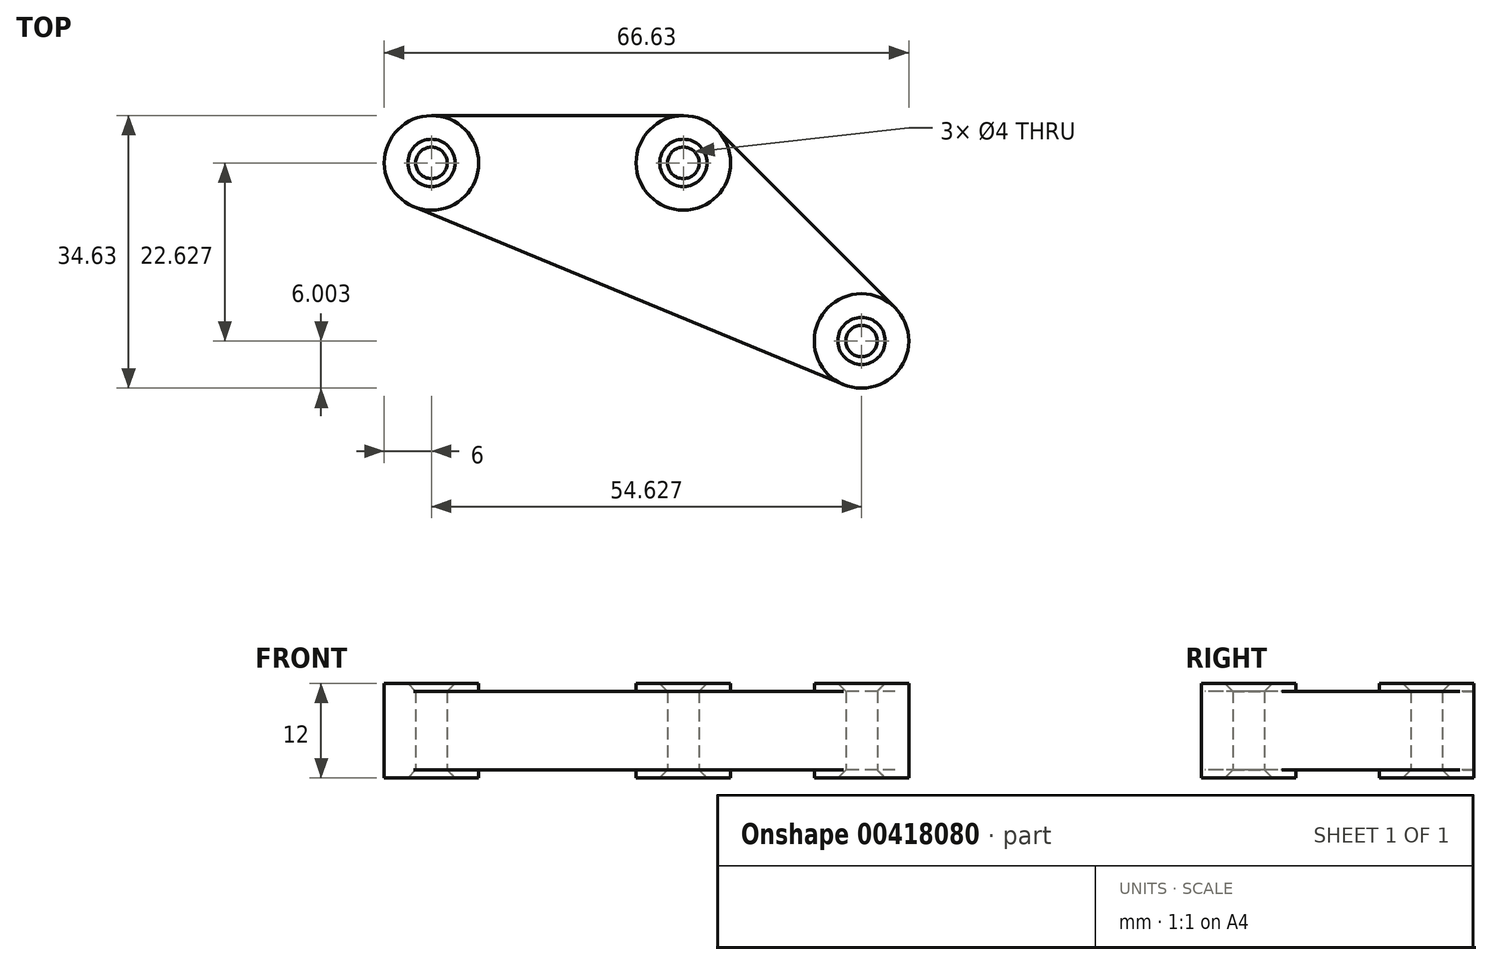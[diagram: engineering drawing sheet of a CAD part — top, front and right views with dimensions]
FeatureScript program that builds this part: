
annotation { "Feature Type Name" : "Feature", "Feature Type Description" : "" }
export const myFeature = defineFeature(function(context is Context, id is Id, definition is map)
    precondition{}
    {
        {
            var Q0;
            Q0=qCreatedBy(makeId("Top.planeOp"),FACE);
            var sketch = newSketch(context, id + "F0", { "sketchPlane" : qUnion([Q0])});
            skCircle(sketch, "E0", {"center": v(0, 0) * mm, "radius": 6 * mm});
            skCircle(sketch, "E1.1.0.0", {"center": v(32, 0) * mm, "radius": 6 * mm});
            skLineSegment(sketch, "E1.direction1", {"start": v(0, 0) * mm, "end": v(32, 0) * mm, "construction": true});
            skCircle(sketch, "E2", {"center": v(0, 0) * mm, "radius": 2 * mm});
            skCircle(sketch, "E3", {"center": v(32, 0) * mm, "radius": 2 * mm});
            skLineSegment(sketch, "E4", {"start": v(0, 0) * mm, "end": v(32, 0) * mm});
            skLineSegment(sketch, "E5", {"start": v(32, 0) * mm, "end": v(54.63, -22.63) * mm});
            skCircle(sketch, "E6", {"center": v(54.63, -22.63) * mm, "radius": 6 * mm});
            skCircle(sketch, "E7", {"center": v(54.63, -22.63) * mm, "radius": 2 * mm});
            skLineSegment(sketch, "E8", {"start": v(-2.3, -5.54) * mm, "end": v(52.33, -28.17) * mm});
            skLineSegment(sketch, "E9", {"start": v(58.87, -18.38) * mm, "end": v(36.24, 4.24) * mm});
            skLineSegment(sketch, "E10", {"start": v(0, 6) * mm, "end": v(32, 6) * mm});
            skSolve(sketch);
        }
        {
            var Q0;
            {var subQ9=sQuery(id+"F0.wireOp",EDGE,"E8");Q0=makeQuery(id+"F0.imprint","IMPRINT",FACE,{"disambiguationData":[TD([[makeQuery(id+"F0.imprint","IMPRINT",EDGE,{"derivedFrom":subQ9}),1.0]])]});}
            var Q1;
            {var subQ0=sQuery(id+"F0.wireOp",EDGE,"E10");Q1=makeQuery(id+"F0.imprint","IMPRINT",FACE,{"disambiguationData":[TD([[makeQuery(id+"F0.imprint","IMPRINT",EDGE,{"derivedFrom":subQ0}),-1.0]])]});}
            var Q2;
            {var subQ0=sQuery(id+"F0.wireOp",EDGE,"E9");Q2=makeQuery(id+"F0.imprint","IMPRINT",FACE,{"disambiguationData":[TD([[makeQuery(id+"F0.imprint","IMPRINT",EDGE,{"derivedFrom":subQ0}),1.0]])]});}
            var Q3;
            Q3=makeQuery(id+"F0.imprint","IMPRINT",FACE,{"disambiguationData":[TD([[makeQuery(id+"F0.imprint","IMPRINT",EDGE,{"derivedFrom":sQuery(id+"F0.wireOp",EDGE,"E2")}),-1.0]])]});
            var Q4;
            {var subQ0=sQuery(id+"F0.wireOp",EDGE,"E4");var subQ1=sQuery(id+"F0.wireOp",EDGE,"E1.1.0.0");var subQ2=makeQuery(id+"F0.imprint","INTERSECT",VERTEX,{"derivedFrom":[subQ1,subQ0]});Q4=makeQuery(id+"F0.imprint","IMPRINT",FACE,{"disambiguationData":[TD([[makeQuery(id+"F0.imprint","IMPRINT",EDGE,{"disambiguationData":[TD([[subQ2,-1.0]])],"derivedFrom":subQ1}),1.0]])]});}
            var Q5;
            {var subQ0=sQuery(id+"F0.wireOp",EDGE,"E1.1.0.0");var subQ1=makeQuery(id+"F0.imprint","INTERSECT",VERTEX,{"derivedFrom":[subQ0,sQuery(id+"F0.wireOp",EDGE,"E9")]});Q5=makeQuery(id+"F0.imprint","IMPRINT",FACE,{"disambiguationData":[TD([[makeQuery(id+"F0.imprint","IMPRINT",EDGE,{"disambiguationData":[TD([[subQ1,-1.0]])],"derivedFrom":subQ0}),1.0]])]});}
            var Q6;
            Q6=makeQuery(id+"F0.imprint","IMPRINT",FACE,{"disambiguationData":[TD([[makeQuery(id+"F0.imprint","IMPRINT",EDGE,{"derivedFrom":sQuery(id+"F0.wireOp",EDGE,"E7")}),-1.0]])]});
            extrude(context, id + "F1", {"entities" : qUnion([Q0, Q1, Q2, Q3, Q4, Q5, Q6]), "depth" : 10 * mm});
        }
        {
            var Q0;
            Q0=makeQuery(id+"F0.imprint","IMPRINT",FACE,{"disambiguationData":[TD([[makeQuery(id+"F0.imprint","IMPRINT",EDGE,{"derivedFrom":sQuery(id+"F0.wireOp",EDGE,"E2")}),-1.0]])]});
            var Q1;
            {var subQ0=sQuery(id+"F0.wireOp",EDGE,"E1.1.0.0");var subQ1=makeQuery(id+"F0.imprint","INTERSECT",VERTEX,{"derivedFrom":[subQ0,sQuery(id+"F0.wireOp",EDGE,"E9")]});Q1=makeQuery(id+"F0.imprint","IMPRINT",FACE,{"disambiguationData":[TD([[makeQuery(id+"F0.imprint","IMPRINT",EDGE,{"disambiguationData":[TD([[subQ1,-1.0]])],"derivedFrom":subQ0}),1.0]])]});}
            var Q2;
            {var subQ0=sQuery(id+"F0.wireOp",EDGE,"E4");var subQ1=sQuery(id+"F0.wireOp",EDGE,"E1.1.0.0");var subQ2=makeQuery(id+"F0.imprint","INTERSECT",VERTEX,{"derivedFrom":[subQ1,subQ0]});Q2=makeQuery(id+"F0.imprint","IMPRINT",FACE,{"disambiguationData":[TD([[makeQuery(id+"F0.imprint","IMPRINT",EDGE,{"disambiguationData":[TD([[subQ2,-1.0]])],"derivedFrom":subQ1}),1.0]])]});}
            var Q3;
            Q3=makeQuery(id+"F0.imprint","IMPRINT",FACE,{"disambiguationData":[TD([[makeQuery(id+"F0.imprint","IMPRINT",EDGE,{"derivedFrom":sQuery(id+"F0.wireOp",EDGE,"E7")}),-1.0]])]});
            extrude(context, id + "F2", {"entities" : qUnion([Q0, Q1, Q2, Q3]), "depth" : 11 * mm});
        }
        {
            var Q0;
            Q0=makeQuery(id+"F0.imprint","IMPRINT",FACE,{"disambiguationData":[TD([[makeQuery(id+"F0.imprint","IMPRINT",EDGE,{"derivedFrom":sQuery(id+"F0.wireOp",EDGE,"E2")}),-1.0]])]});
            var Q1;
            {var subQ0=sQuery(id+"F0.wireOp",EDGE,"E1.1.0.0");var subQ1=makeQuery(id+"F0.imprint","INTERSECT",VERTEX,{"derivedFrom":[subQ0,sQuery(id+"F0.wireOp",EDGE,"E9")]});Q1=makeQuery(id+"F0.imprint","IMPRINT",FACE,{"disambiguationData":[TD([[makeQuery(id+"F0.imprint","IMPRINT",EDGE,{"disambiguationData":[TD([[subQ1,-1.0]])],"derivedFrom":subQ0}),1.0]])]});}
            var Q2;
            {var subQ0=sQuery(id+"F0.wireOp",EDGE,"E4");var subQ1=sQuery(id+"F0.wireOp",EDGE,"E1.1.0.0");var subQ2=makeQuery(id+"F0.imprint","INTERSECT",VERTEX,{"derivedFrom":[subQ1,subQ0]});Q2=makeQuery(id+"F0.imprint","IMPRINT",FACE,{"disambiguationData":[TD([[makeQuery(id+"F0.imprint","IMPRINT",EDGE,{"disambiguationData":[TD([[subQ2,-1.0]])],"derivedFrom":subQ1}),1.0]])]});}
            var Q3;
            Q3=makeQuery(id+"F0.imprint","IMPRINT",FACE,{"disambiguationData":[TD([[makeQuery(id+"F0.imprint","IMPRINT",EDGE,{"derivedFrom":sQuery(id+"F0.wireOp",EDGE,"E7")}),-1.0]])]});
            extrude(context, id + "F3", {"entities" : qUnion([Q0, Q1, Q2, Q3]), "operationType" : NewBodyOperationType.ADD, "depth" : -1 * mm});
        }
        {
            var Q0;
            Q0=makeQuery(id+"F2.opExtrude","CAP_EDGE",EDGE,{"disambiguationData":[OSD([sQuery(id+"F0.wireOp",EDGE,"E2")])],"isStart":false});
            var Q1;
            Q1=makeQuery(id+"F2.opExtrude","CAP_EDGE",EDGE,{"disambiguationData":[OSD([sQuery(id+"F0.wireOp",EDGE,"E3")])],"isStart":false});
            var Q2;
            Q2=makeQuery(id+"F2.opExtrude","CAP_EDGE",EDGE,{"disambiguationData":[OSD([sQuery(id+"F0.wireOp",EDGE,"E7")])],"isStart":false});
            var Q3;
            Q3=makeQuery(id+"F3.opExtrude","CAP_EDGE",EDGE,{"disambiguationData":[OSD([sQuery(id+"F0.wireOp",EDGE,"E2")])],"isStart":false});
            var Q4;
            Q4=makeQuery(id+"F3.opExtrude","CAP_EDGE",EDGE,{"disambiguationData":[OSD([sQuery(id+"F0.wireOp",EDGE,"E3")])],"isStart":false});
            var Q5;
            Q5=makeQuery(id+"F3.opExtrude","CAP_EDGE",EDGE,{"disambiguationData":[OSD([sQuery(id+"F0.wireOp",EDGE,"E7")])],"isStart":false});
            chamfer(context, id + "F4", {"entities" : qUnion([Q0, Q1, Q2, Q3, Q4, Q5]), "width" : 1 * mm, "tangentPropagation" : true});
        }
    });
